# Revit family: 105900038
name_source: partatom
category: Furniture
units: mm (PartAtom-declared; Revit-internal decimal feet)

## family parameters
Always vertical = Yes
Cut with Voids When Loaded = No
OmniClass Number = 23.40.20.00
OmniClass Title = General Furniture and Specialties
Room Calculation Point = No
Shared = No
Work Plane-Based = No

## types (1)
- Sykkelstativ_U800-1000-800_inklTverrligger_Default_As Machined_
    Artnr = 07-500-???
    CheckedDate_Config = -
    CheckedDate_Custom = -
    Default Elevation = 0 mm  [stored 0 ft]
    Material = S235JRH
    Number_Config = 117878
    Number_Custom = 117878
    PartName_Config = Sykkelstativ_JP_U800-1000-800
    PartName_Custom = Sykkelstativ_JP_U800-1000-800
    Revision_Config = 0
    Revision_Custom = 0
    Weight = 10.26

note: [stored X ft] marks values corroborated as IEEE doubles in the binary element streams (Revit-internal decimal feet)

## geometry (parser evidence)
native form markers: Sweep x3
no freeform markers — native parametric forms only
